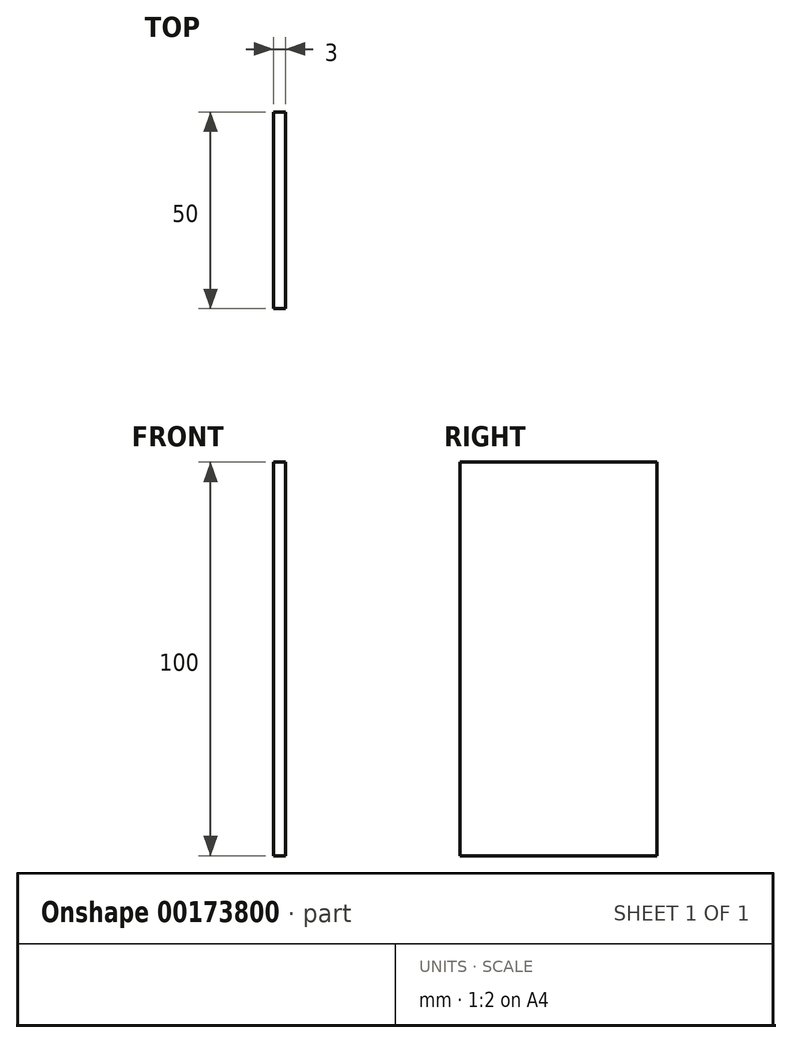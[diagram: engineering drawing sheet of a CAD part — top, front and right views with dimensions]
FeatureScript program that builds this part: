
annotation { "Feature Type Name" : "Feature", "Feature Type Description" : "" }
export const myFeature = defineFeature(function(context is Context, id is Id, definition is map)
    precondition{}
    {
        {
            var Q0;
            Q0=qCreatedBy(makeId("Front.planeOp"),FACE);
            var sketch = newSketch(context, id + "F0", { "sketchPlane" : qUnion([Q0])});
            skLineSegment(sketch, "E0", {"start": v(0, 66.97) * mm, "end": v(0, -33.03) * mm});
            skLineSegment(sketch, "E1", {"start": v(0, 66.97) * mm, "end": v(1.5, 66.97) * mm});
            skLineSegment(sketch, "E2", {"start": v(1.5, 66.97) * mm, "end": v(1.5, -33.03) * mm});
            skLineSegment(sketch, "E3", {"start": v(1.5, -33.03) * mm, "end": v(0, -33.03) * mm});
            skLineSegment(sketch, "E4", {"start": v(0, 66.97) * mm, "end": v(-1.5, 66.97) * mm});
            skLineSegment(sketch, "E5", {"start": v(-1.5, 66.97) * mm, "end": v(-1.5, -33.03) * mm});
            skLineSegment(sketch, "E6", {"start": v(-1.5, -33.03) * mm, "end": v(0, -33.03) * mm});
            skSolve(sketch);
        }
        {
            var Q0;
            Q0=makeQuery(id+"F0.imprint","IMPRINT",FACE,{"disambiguationData":[TD([[makeQuery(id+"F0.imprint","IMPRINT",EDGE,{"derivedFrom":sQuery(id+"F0.wireOp",EDGE,"E0")}),1.0]])]});
            var Q1;
            Q1=makeQuery(id+"F0.imprint","IMPRINT",FACE,{"disambiguationData":[TD([[makeQuery(id+"F0.imprint","IMPRINT",EDGE,{"derivedFrom":sQuery(id+"F0.wireOp",EDGE,"E0")}),-1.0]])]});
            extrude(context, id + "F1", {"entities" : qUnion([Q0, Q1]), "endBound" : BoundingType.SYMMETRIC, "depth" : 50 * mm});
        }
    });
